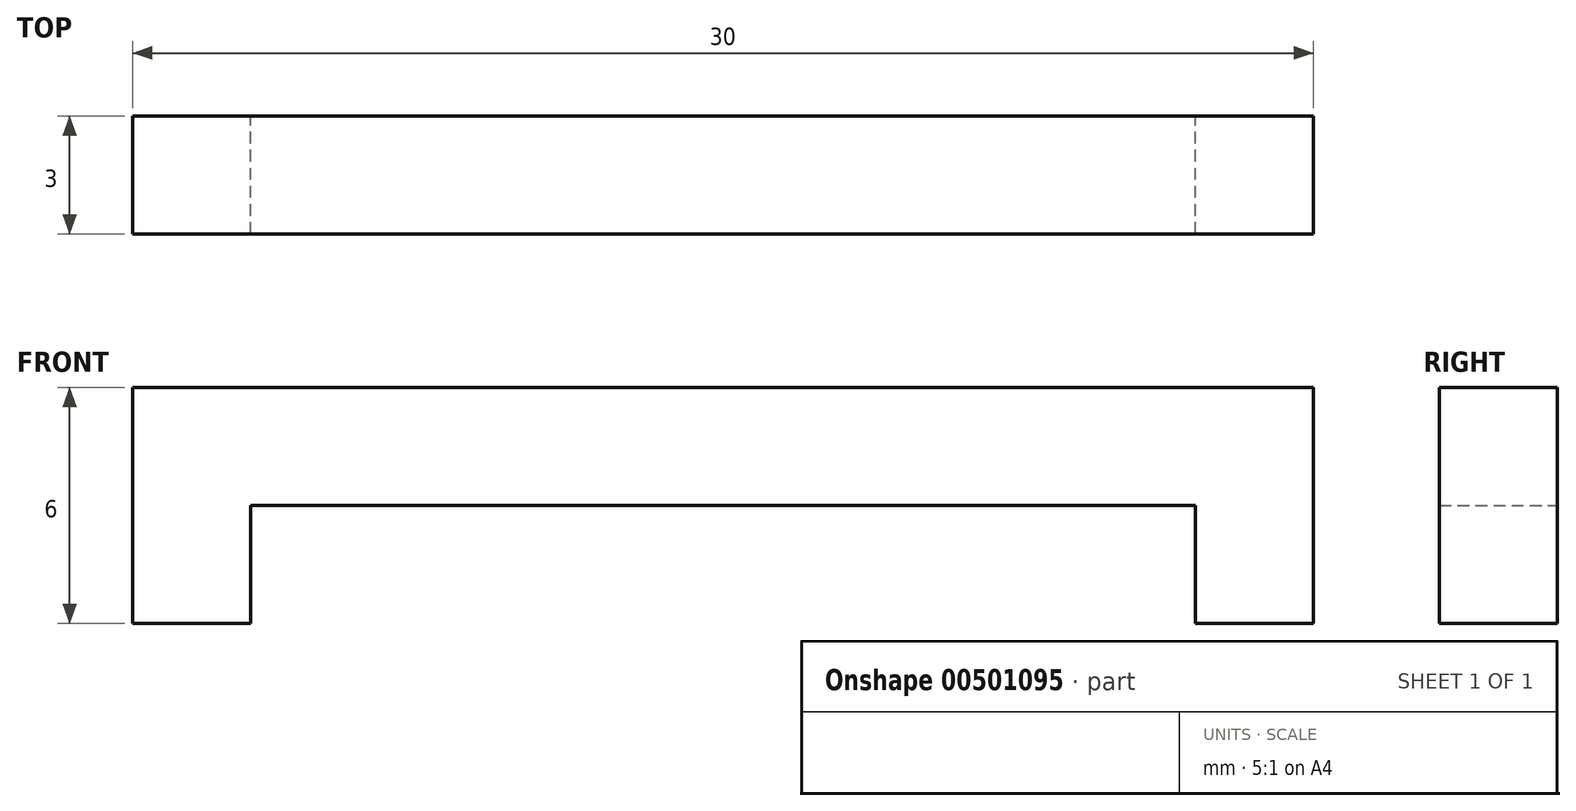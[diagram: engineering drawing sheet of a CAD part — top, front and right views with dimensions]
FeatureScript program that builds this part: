
annotation { "Feature Type Name" : "Feature", "Feature Type Description" : "" }
export const myFeature = defineFeature(function(context is Context, id is Id, definition is map)
    precondition{}
    {
        {
            var Q0;
            Q0=qCreatedBy(makeId("Front.planeOp"),FACE);
            var sketch = newSketch(context, id + "F0", { "sketchPlane" : qUnion([Q0])});
            skLineSegment(sketch, "E0", {"start": v(-18.29, 0) * mm, "end": v(-18.29, 6) * mm});
            skLineSegment(sketch, "E1", {"start": v(-18.29, 6) * mm, "end": v(11.71, 6) * mm});
            skLineSegment(sketch, "E2", {"start": v(11.71, 6) * mm, "end": v(11.71, 0) * mm});
            skLineSegment(sketch, "E3", {"start": v(11.71, 0) * mm, "end": v(8.71, 0) * mm});
            skLineSegment(sketch, "E4", {"start": v(8.71, 0) * mm, "end": v(8.71, 3) * mm});
            skLineSegment(sketch, "E5", {"start": v(8.71, 3) * mm, "end": v(-15.29, 3) * mm});
            skLineSegment(sketch, "E6", {"start": v(-15.29, 3) * mm, "end": v(-15.29, 0) * mm});
            skLineSegment(sketch, "E7", {"start": v(-15.29, 0) * mm, "end": v(-18.29, 0) * mm});
            skSolve(sketch);
        }
        {
            var Q0;
            Q0=makeQuery(id+"F0.imprint","IMPRINT",FACE,{"disambiguationData":[TD([[makeQuery(id+"F0.imprint","IMPRINT",EDGE,{"derivedFrom":sQuery(id+"F0.wireOp",EDGE,"E0")}),-1.0]])]});
            extrude(context, id + "F1", {"entities" : qUnion([Q0]), "depth" : 3 * mm});
        }
    });
